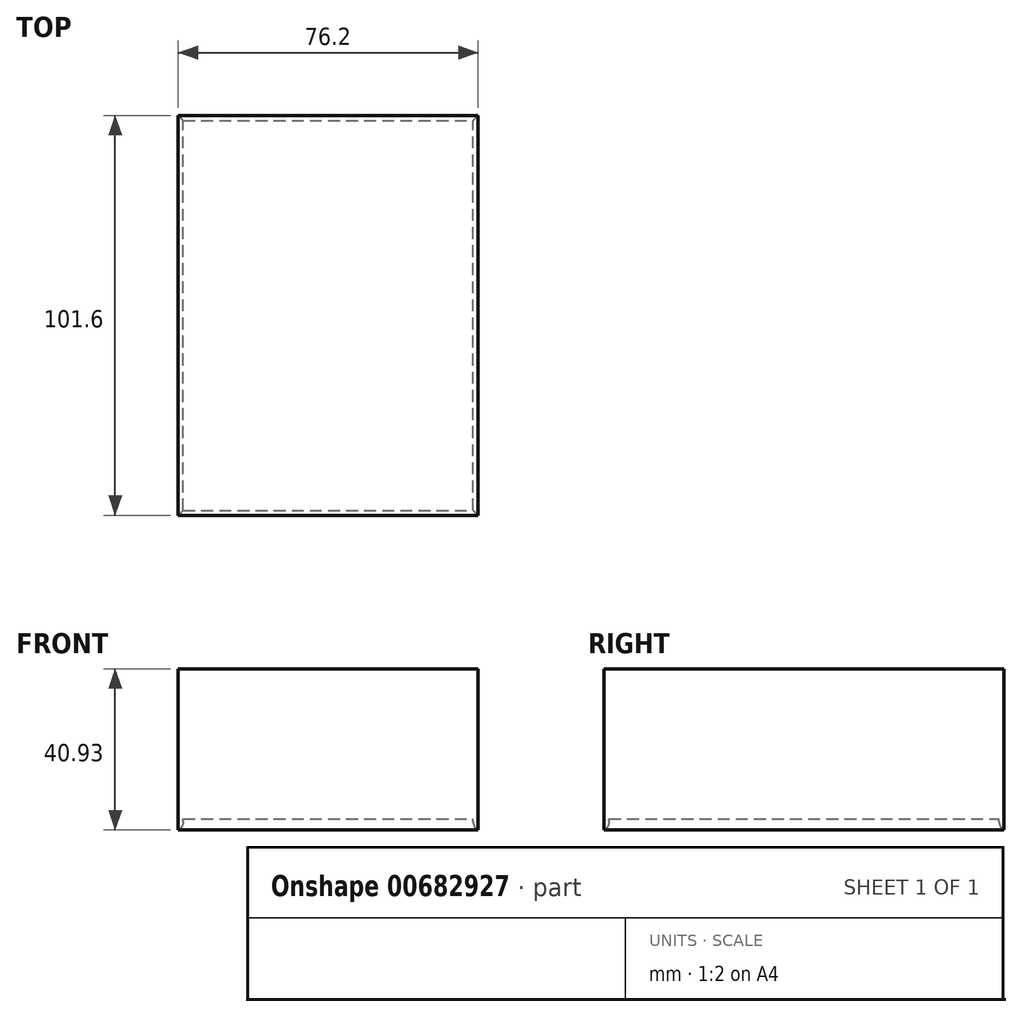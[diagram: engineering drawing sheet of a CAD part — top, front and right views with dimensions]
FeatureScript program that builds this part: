
annotation { "Feature Type Name" : "Feature", "Feature Type Description" : "" }
export const myFeature = defineFeature(function(context is Context, id is Id, definition is map)
    precondition{}
    {
        {
            var Q0;
            Q0=qCreatedBy(makeId("Top.planeOp"),FACE);
            var sketch = newSketch(context, id + "F0", { "sketchPlane" : qUnion([Q0])});
            skLineSegment(sketch, "E0.bottom", {"start": v(38.1, 50.8) * mm, "end": v(-38.1, 50.8) * mm});
            skLineSegment(sketch, "E0.top", {"start": v(38.1, -50.8) * mm, "end": v(-38.1, -50.8) * mm});
            skLineSegment(sketch, "E0.left", {"start": v(38.1, 50.8) * mm, "end": v(38.1, -50.8) * mm});
            skLineSegment(sketch, "E0.right", {"start": v(-38.1, 50.8) * mm, "end": v(-38.1, -50.8) * mm});
            skPoint(sketch, "E0.middle", {"position": v(0, 0) * mm});
            skSolve(sketch);
        }
        {
            var Q0;
            Q0=qSketchRegion(id+"F0",true);
            extrude(context, id + "F1", {"entities" : qUnion([Q0]), "depth" : 38.1 * mm, "offsetDistance" : 25.4 * mm});
        }
        {
            var Q0;
            Q0=makeQuery(id+"F1.opExtrude","CAP_FACE",FACE,{"disambiguationData":[OSD([sQuery(id+"F0.wireOp",EDGE,"E0.bottom"),sQuery(id+"F0.wireOp",EDGE,"E0.top"),sQuery(id+"F0.wireOp",EDGE,"E0.left"),sQuery(id+"F0.wireOp",EDGE,"E0.right")])],"isStart":false});
            var sketch = newSketch(context, id + "F2", { "sketchPlane" : qUnion([Q0])});
            skLineSegment(sketch, "E1.top", {"start": v(-36.2, -48.9) * mm, "end": v(36.2, -48.9) * mm});
            skLineSegment(sketch, "E1.right", {"start": v(36.2, 48.9) * mm, "end": v(36.2, -48.9) * mm});
            skPoint(sketch, "E1.middle", {"position": v(0, 0) * mm});
            skLineSegment(sketch, "E2.bottom", {"start": v(-34.92, 47.63) * mm, "end": v(34.92, 47.63) * mm});
            skLineSegment(sketch, "E2.top", {"start": v(-34.92, -47.63) * mm, "end": v(34.92, -47.63) * mm});
            skLineSegment(sketch, "E2.left", {"start": v(-34.92, 47.63) * mm, "end": v(-34.92, -47.63) * mm});
            skLineSegment(sketch, "E2.right", {"start": v(34.92, 47.63) * mm, "end": v(34.92, -47.63) * mm});
            skSolve(sketch);
        }
        {
            var Q0;
            Q0=makeQuery(id+"F1.opExtrude","CAP_FACE",FACE,{"disambiguationData":[OSD([sQuery(id+"F0.wireOp",EDGE,"E0.bottom"),sQuery(id+"F0.wireOp",EDGE,"E0.top"),sQuery(id+"F0.wireOp",EDGE,"E0.left"),sQuery(id+"F0.wireOp",EDGE,"E0.right")])],"isStart":true});
            var sketch = newSketch(context, id + "F3", { "sketchPlane" : qUnion([Q0])});
            skLineSegment(sketch, "E3.bottom", {"start": v(-36.83, 49.53) * mm, "end": v(36.83, 49.53) * mm});
            skLineSegment(sketch, "E3.top", {"start": v(-36.83, -49.53) * mm, "end": v(36.83, -49.53) * mm});
            skLineSegment(sketch, "E3.left", {"start": v(-36.83, 49.53) * mm, "end": v(-36.83, -49.53) * mm});
            skLineSegment(sketch, "E3.right", {"start": v(36.83, 49.53) * mm, "end": v(36.83, -49.53) * mm});
            skPoint(sketch, "E3.middle", {"position": v(0, 0) * mm});
            skLineSegment(sketch, "E4.bottom", {"start": v(-38.1, 50.8) * mm, "end": v(38.1, 50.8) * mm});
            skLineSegment(sketch, "E4.top", {"start": v(-38.1, -50.8) * mm, "end": v(38.1, -50.8) * mm});
            skLineSegment(sketch, "E4.left", {"start": v(-38.1, 50.8) * mm, "end": v(-38.1, -50.8) * mm});
            skLineSegment(sketch, "E4.right", {"start": v(38.1, 50.8) * mm, "end": v(38.1, -50.8) * mm});
            skSolve(sketch);
        }
        {
            var Q0;
            Q0=qSketchRegion(id+"F3",true);
            extrude(context, id + "F4", {"entities" : qUnion([Q0]), "operationType" : NewBodyOperationType.ADD, "depth" : 3.17 * mm, "offsetDistance" : 25.4 * mm});
        }
        {
            var Q0;
            Q0=makeQuery(id+"FcFGXfjceB7BRWR_1.opExtrude","CAP_EDGE",EDGE,{"disambiguationData":[OSD([sQuery(id+"F2.wireOp",EDGE,"E1.left")])],"isStart":false});
            var Q1;
            Q1=makeQuery(id+"FcFGXfjceB7BRWR_1.opExtrude","CAP_EDGE",EDGE,{"disambiguationData":[OSD([sQuery(id+"F2.wireOp",EDGE,"E1.top")])],"isStart":false});
            var Q2;
            Q2=makeQuery(id+"FcFGXfjceB7BRWR_1.opExtrude","CAP_EDGE",EDGE,{"disambiguationData":[OSD([sQuery(id+"F2.wireOp",EDGE,"E1.right")])],"isStart":false});
            var Q3;
            Q3=makeQuery(id+"FcFGXfjceB7BRWR_1.opExtrude","CAP_EDGE",EDGE,{"disambiguationData":[OSD([sQuery(id+"F2.wireOp",EDGE,"E1.bottom")])],"isStart":false});
            var Q4;
            Q4=makeQuery(id+"F4.opExtrude","CAP_EDGE",EDGE,{"disambiguationData":[OSD([sQuery(id+"F3.wireOp",EDGE,"E3.left")])],"isStart":false});
            var Q5;
            Q5=makeQuery(id+"F4.opExtrude","CAP_EDGE",EDGE,{"disambiguationData":[OSD([sQuery(id+"F3.wireOp",EDGE,"E3.bottom")])],"isStart":false});
            var Q6;
            Q6=makeQuery(id+"F4.opExtrude","CAP_EDGE",EDGE,{"disambiguationData":[OSD([sQuery(id+"F3.wireOp",EDGE,"E3.right")])],"isStart":false});
            var Q7;
            Q7=makeQuery(id+"F4.opExtrude","CAP_EDGE",EDGE,{"disambiguationData":[OSD([sQuery(id+"F3.wireOp",EDGE,"E3.top")])],"isStart":false});
            fillet(context, id + "F5", {"entities" : qUnion([Q0, Q1, Q2, Q3, Q4, Q5, Q6, Q7]), "radius" : 2.54 * mm, "tangentPropagation" : true, "allowEdgeOverflow" : false});
        }
    });
